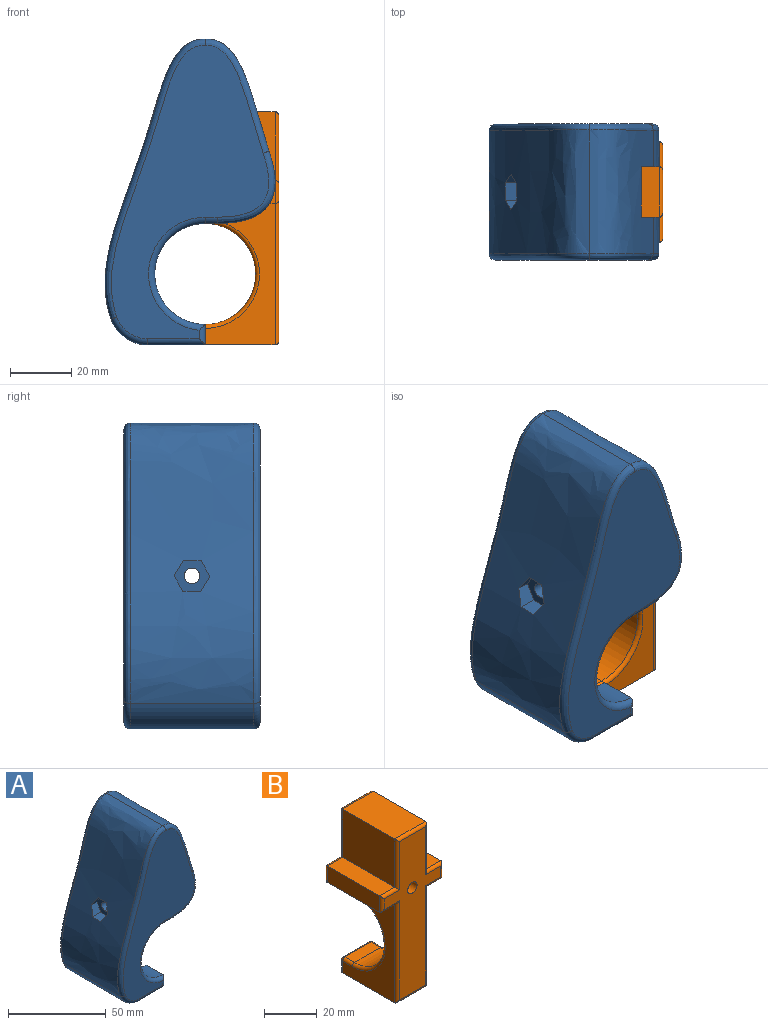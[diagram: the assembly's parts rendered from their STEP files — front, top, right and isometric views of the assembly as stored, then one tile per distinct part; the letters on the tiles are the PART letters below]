
ASSEMBLY  parts=2 mates=1
PART A: 52 faces, bbox 64.6x51.9x104.1 mm
  f0: extruded ~91.6x40.39mm, area 4018.1mm2, adj f7,f14,f22,f27,f45,f46,f47,f48
  f1: plane 11.94x6.69mm, normal (1,0,0), area 79.8mm2, adj f2,f9,f13,f43
  f2: plane 40.39x18.87mm, normal (0,0,-1), area 552.3mm2, adj f1,f10,f12,f20,f27,f41,f42,f43
  f3: plane 11.94x3.9mm, normal (0,0,-1), area 46.5mm2, adj f4,f9,f23,f30
  f4: bspline ~48.9x24.91mm, area 373.3mm2, adj f3,f7,f25,f29,f30,f33,f34,f35
  f5: plane 95.92x51.47mm, normal (0,-1,0), area 2385.3mm2, adj f19,f20,f21,f22,f23,f24,f25,f26
  f6: plane 95.92x51.47mm, normal (0,1,0), area 2385.3mm2, adj f12,f13,f14,f15,f16,f17,f18,f28
  f7: extruded ~40.39x36.67mm, area 1588.8mm2, adj f0,f4,f11,f16,f24,f29,f32,f39
  f8: plane 11.94x3.9mm, normal (0,0,-1), area 46.5mm2, adj f9,f11,f17,f31
  f9: cylinder r=16.51mm len=40.39mm, axis (0,1,0), area 1616.3mm2, adj f1,f3,f8,f10,f15,f21,f30,f31
  f10: plane 11.94x6.69mm, normal (1,0,0), area 79.8mm2, adj f2,f9,f19,f42
  f11: bspline ~48.9x24.91mm, area 373.3mm2, adj f7,f8,f18,f31,f32,f36,f37,f38
  f12: cylinder r=2.03mm len=18.87mm, axis (1,0,0), area 57mm2, adj f2,f6,f13,f28
  f13: cylinder r=2.03mm len=6.69mm, axis (0,0,1), area 15mm2, adj f1,f6,f12,f15
  f14: bspline ~94.05x34.21mm, area 320.6mm2, adj f0,f6,f16,f28
  f15: torus R=18.54mm, axis (0,-1,0), area 169.9mm2, adj f6,f9,f13,f17
  f16: bspline ~43.22x23.16mm, area 140.3mm2, adj f6,f7,f14,f18
  f17: cylinder r=2.03mm len=3.9mm, axis (1,0,0), area 12.4mm2, adj f6,f8,f15,f18
  f18: bspline ~34.23x30.1mm, area 112.8mm2, adj f6,f11,f16,f17
  f19: cylinder r=2.03mm len=6.69mm, axis (0,0,1), area 15mm2, adj f5,f10,f20,f21
  f20: cylinder r=2.03mm len=18.87mm, axis (-1,0,0), area 57mm2, adj f2,f5,f19,f26
  f21: torus R=18.54mm, axis (0,-1,0), area 169.9mm2, adj f5,f9,f19,f23
  f22: bspline ~92.57x34.21mm, area 320.6mm2, adj f0,f5,f24,f26
  f23: cylinder r=2.03mm len=3.9mm, axis (1,0,0), area 12.4mm2, adj f3,f5,f21,f25
  f24: bspline ~43.22x23.16mm, area 140.3mm2, adj f5,f7,f22,f25
  f25: bspline ~34.23x30.1mm, area 112.8mm2, adj f4,f5,f23,f24
  f26: torus R=10.67mm, axis (0,-1,0), area 46.7mm2, adj f5,f20,f22,f27
  f27: cylinder r=12.7mm len=40.39mm, axis (0,1,0), area 627.7mm2, adj f0,f2,f26,f28
  f28: torus R=10.67mm, axis (0,-1,0), area 46.7mm2, adj f6,f12,f14,f27
  f29: plane 36.24x23.18mm, normal (0,1,0), area 737.2mm2, adj f4,f7,f33,f39,f40
  f30: plane 36.68x15.44mm, normal (0,1,0), area 213.7mm2, adj f3,f4,f9,f35,f40
  f31: plane 36.68x15.44mm, normal (0,-1,0), area 213.7mm2, adj f8,f9,f11,f36,f40
  f32: plane 36.24x23.18mm, normal (0,-1,0), area 737.2mm2, adj f7,f11,f38,f39,f40
  f33: plane 35.47x8.21mm, normal (0,0,-1), area 291.3mm2, adj f4,f29,f34,f40
  f34: plane 35.95x8.08mm, normal (0,1,0), area 266.4mm2, adj f4,f33,f35,f40
  f35: plane 33.67x8.21mm, normal (0,0,1), area 276.5mm2, adj f4,f30,f34,f40
  f36: plane 33.67x8.21mm, normal (0,0,1), area 276.5mm2, adj f11,f31,f37,f40
  f37: plane 35.95x8.08mm, normal (0,-1,0), area 266.4mm2, adj f11,f36,f38,f40
  f38: plane 35.47x8.21mm, normal (0,0,-1), area 291.3mm2, adj f11,f32,f37,f40
  f39: plane 29.61x16.51mm, normal (0,0,-1), area 488.8mm2, adj f7,f29,f32,f40
  f40: plane 42.45x32.93mm, normal (1,0,0), area 805.8mm2, adj f9,f29,f30,f31,f32,f33,f34,f35
  f41: plane 16.51x12.65mm, normal (1,0,0), area 208.8mm2, adj f2,f9,f42,f43
  f42: plane 12.7x12.65mm, normal (0,1,0), area 108mm2, adj f2,f9,f10,f41
  f43: plane 12.7x12.65mm, normal (0,-1,0), area 108mm2, adj f1,f2,f9,f41
  f44: cylinder r=2.54mm len=8.89mm, axis (1,0,0), area 141.9mm2, adj f40,f51
  f45: plane 5.84x5.16mm, normal (0,-0.87,0.49), area 28.6mm2, adj f0,f46,f50,f51
  f46: plane 5.06x4.01mm, normal (0,-0.86,-0.51), area 17.9mm2, adj f0,f45,f47,f51
  f47: plane 5.85x2.19mm, normal (0,0.02,-1), area 12.7mm2, adj f0,f46,f48,f51
  f48: plane 5.15x4.08mm, normal (0,0.87,-0.49), area 18.2mm2, adj f0,f47,f49,f51
  f49: plane 5.87x5.06mm, normal (0,0.86,0.51), area 28.9mm2, adj f0,f48,f50,f51
  f50: plane 5.85x5.83mm, normal (0,-0.02,1), area 34mm2, adj f0,f45,f49,f51
  f51: plane 11.7x10.23mm, normal (-1,0,0), area 68.7mm2, adj f44,f45,f46,f47,f48,f49,f50
PART B: 56 faces, bbox 32.9x30.5x76.2 mm
  f0: plane 33.95x30.39mm, normal (0,1,0), area 537.5mm2, adj f19,f26,f27,f28,f29,f30,f31,f32
  f1: plane 27.94x22.41mm, normal (-1,0,0), area 626.1mm2, adj f2,f12,f32,f53
  f2: plane 27.94x8.21mm, normal (0,0,1), area 229.5mm2, adj f1,f3,f33,f51
  f3: plane 27.94x7.62mm, normal (-1,0,0), area 212.9mm2, adj f2,f4,f34,f49
  f4: plane 27.94x8.21mm, normal (0,0,-1), area 229.5mm2, adj f3,f5,f35,f47
  f5: plane 46.17x27.94mm, normal (-1,0,0), area 612.8mm2, adj f4,f6,f36,f38,f39,f40,f42,f45
  f6: plane 29.21x16.51mm, normal (0,0,-1), area 481.6mm2, adj f5,f7,f14,f20,f42,f43
  f7: plane 46.17x27.94mm, normal (1,0,0), area 612.8mm2, adj f6,f8,f20,f22,f23,f24,f26,f44
  f8: plane 27.94x8.21mm, normal (0,0,-1), area 229.5mm2, adj f7,f9,f27,f46
  f9: plane 27.94x7.62mm, normal (1,0,0), area 212.9mm2, adj f8,f10,f28,f48
  f10: plane 27.94x8.21mm, normal (0,0,1), area 229.5mm2, adj f9,f11,f29,f50
  f11: plane 27.94x22.41mm, normal (1,0,0), area 626.1mm2, adj f10,f12,f30,f52
  f12: plane 27.94x16.51mm, normal (0,0,1), area 461.3mm2, adj f1,f11,f31,f54
  f13: plane 73.66x30.39mm, normal (0,-1,0), area 1092.2mm2, adj f43,f44,f45,f46,f47,f48,f49,f50
  f14: plane 13.97x5.42mm, normal (0,1,0), area 75.7mm2, adj f6,f18,f20,f42
  f15: cylinder r=16.51mm len=33.02mm, axis (1,0,0), area 724.6mm2, adj f16,f17,f23,f39
  f16: plane 13.97x5.08mm, normal (0,0,1), area 71mm2, adj f15,f18,f22,f40
  f17: plane 13.97x5.08mm, normal (0,0,-1), area 71mm2, adj f15,f19,f24,f38
  f18: cylinder r=1.27mm len=13.97mm, axis (1,0,0), area 27.9mm2, adj f14,f16,f21,f41
  f19: cylinder r=1.27mm len=13.97mm, axis (-1,0,0), area 27.9mm2, adj f0,f17,f25,f37
  f20: cylinder r=1.27mm len=5.42mm, axis (0,0,1), area 10.8mm2, adj f6,f7,f14,f21
  f21: sphere r=1.27mm, area 2.5mm2, adj f18,f20,f22
  f22: cylinder r=1.27mm len=5.08mm, axis (0,-1,0), area 10.1mm2, adj f7,f16,f21,f23
  f23: torus R=17.78mm, axis (1,0,0), area 106.4mm2, adj f7,f15,f22,f24
  f24: cylinder r=1.27mm len=5.08mm, axis (0,1,0), area 10.1mm2, adj f7,f17,f23,f25
  f25: sphere r=1.27mm, area 2.5mm2, adj f19,f24,f26
  f26: cylinder r=1.27mm len=6.47mm, axis (0,0,1), area 11.3mm2, adj f0,f7,f25,f27
  f27: cylinder r=1.27mm len=9.48mm, axis (1,0,0), area 16.4mm2, adj f0,f8,f26,f28
  f28: cylinder r=1.27mm len=7.62mm, axis (0,0,1), area 13.4mm2, adj f0,f9,f27,f29
  f29: cylinder r=1.27mm len=9.48mm, axis (-1,0,0), area 16.4mm2, adj f0,f10,f28,f30
  f30: cylinder r=1.27mm len=23.68mm, axis (0,0,1), area 44.7mm2, adj f0,f11,f29,f31
  f31: cylinder r=1.27mm len=16.51mm, axis (-1,0,0), area 31.1mm2, adj f0,f12,f30,f32
  f32: cylinder r=1.27mm len=23.68mm, axis (0,0,-1), area 44.7mm2, adj f0,f1,f31,f33
  f33: cylinder r=1.27mm len=9.48mm, axis (-1,0,0), area 16.4mm2, adj f0,f2,f32,f34
  f34: cylinder r=1.27mm len=7.62mm, axis (0,0,-1), area 13.4mm2, adj f0,f3,f33,f35
  f35: cylinder r=1.27mm len=9.48mm, axis (1,0,0), area 16.4mm2, adj f0,f4,f34,f36
  f36: cylinder r=1.27mm len=6.47mm, axis (0,0,-1), area 11.3mm2, adj f0,f5,f35,f37
  f37: sphere r=1.27mm, area 2.5mm2, adj f19,f36,f38
  f38: cylinder r=1.27mm len=5.08mm, axis (0,-1,0), area 10.1mm2, adj f5,f17,f37,f39
  f39: torus R=17.78mm, axis (1,0,0), area 106.4mm2, adj f5,f15,f38,f40
  f40: cylinder r=1.27mm len=5.08mm, axis (0,1,0), area 10.1mm2, adj f5,f16,f39,f41
  f41: sphere r=1.27mm, area 2.5mm2, adj f18,f40,f42
  f42: cylinder r=1.27mm len=5.42mm, axis (0,0,-1), area 10.8mm2, adj f5,f6,f14,f41
  f43: cylinder r=1.27mm len=16.51mm, axis (-1,0,0), area 31.1mm2, adj f6,f13,f44,f45
  f44: cylinder r=1.27mm len=47.44mm, axis (0,0,-1), area 92.1mm2, adj f7,f13,f43,f46
  f45: cylinder r=1.27mm len=47.44mm, axis (0,0,1), area 92.1mm2, adj f5,f13,f43,f47
  f46: cylinder r=1.27mm len=9.48mm, axis (-1,0,0), area 16.4mm2, adj f8,f13,f44,f48
  f47: cylinder r=1.27mm len=9.48mm, axis (-1,0,0), area 16.4mm2, adj f4,f13,f45,f49
  f48: cylinder r=1.27mm len=7.62mm, axis (0,0,-1), area 13.4mm2, adj f9,f13,f46,f50
  f49: cylinder r=1.27mm len=7.62mm, axis (0,0,1), area 13.4mm2, adj f3,f13,f47,f51
  f50: cylinder r=1.27mm len=9.48mm, axis (1,0,0), area 16.4mm2, adj f10,f13,f48,f52
  f51: cylinder r=1.27mm len=9.48mm, axis (1,0,0), area 16.4mm2, adj f2,f13,f49,f53
  f52: cylinder r=1.27mm len=23.68mm, axis (0,0,-1), area 44.7mm2, adj f11,f13,f50,f54
  f53: cylinder r=1.27mm len=23.68mm, axis (0,0,1), area 44.7mm2, adj f1,f13,f51,f54
  f54: cylinder r=1.27mm len=16.51mm, axis (1,0,0), area 31.1mm2, adj f12,f13,f52,f53
  f55: cylinder r=2.54mm len=30.48mm, axis (0,1,0), area 486.4mm2, adj f0,f13
PLACE A t=(-32.64,40.02,-32.22)mm fixed
PLACE B rot(axis=(0,0,1),90deg) t=(-39.07,17.8,-4.5)mm
MATE slider B.f55 <-> A.f44  axis (-1,0,0) through (-39.07,17.8,-5.44)mm
